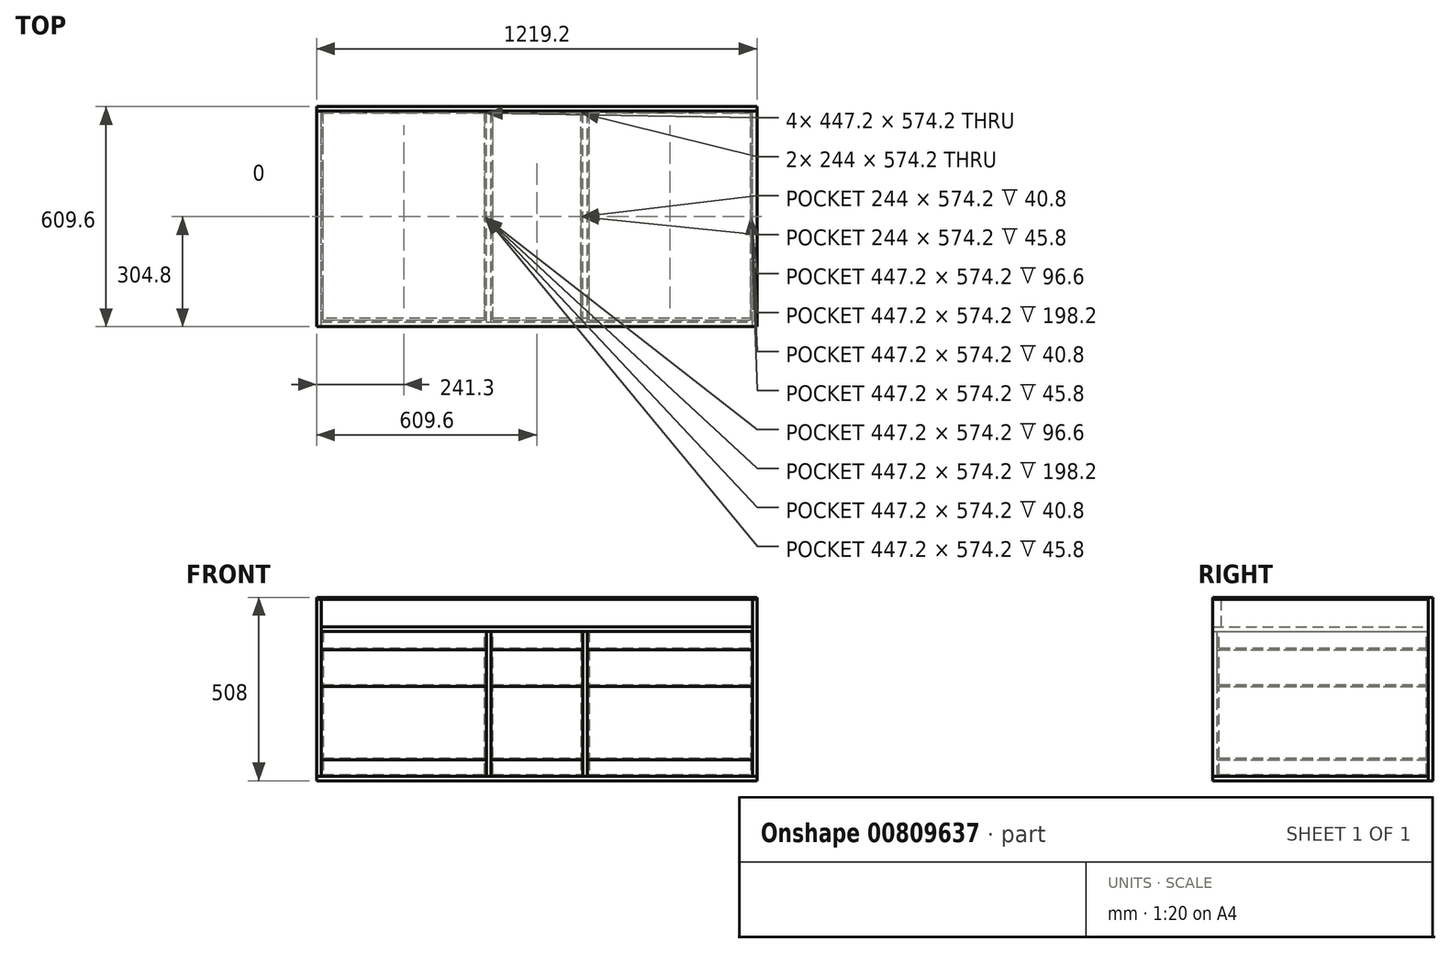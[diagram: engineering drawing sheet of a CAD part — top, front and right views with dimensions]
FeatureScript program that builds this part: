
annotation { "Feature Type Name" : "Feature", "Feature Type Description" : "" }
export const myFeature = defineFeature(function(context is Context, id is Id, definition is map)
    precondition{}
    {
        {
            assignVariable(context, id + "F0", {"name" : "thinwood", "anyValue" : 5 * mm});
        }
        {
            assignVariable(context, id + "F1", {"name" : "thickwood", "anyValue" : 12.7 * mm});
        }
        {
            assignVariable(context, id + "F2", {"name" : "cartlength", "anyValue" : 1219.2 * mm});
        }
        {
            assignVariable(context, id + "F3", {"name" : "cartwidth", "anyValue" : 609.6 * mm});
        }
        {
            assignVariable(context, id + "F4", {"name" : "drawerdepth", "anyValue" : getVariable(context, 'cartwidth') - 2 * getVariable(context, 'thickwood')});
        }
        {
            var Q0;
            Q0=qCreatedBy(makeId("Front.planeOp"),FACE);
            var sketch = newSketch(context, id + "F5", { "sketchPlane" : qUnion([Q0])});
            skLineSegment(sketch, "E0.bottom", {"start": v(609.6, 254) * mm, "end": v(-609.6, 254) * mm});
            skLineSegment(sketch, "E0.top", {"start": v(609.6, -254) * mm, "end": v(-609.6, -254) * mm});
            skLineSegment(sketch, "E0.left", {"start": v(609.6, 254) * mm, "end": v(609.6, -254) * mm});
            skLineSegment(sketch, "E0.right", {"start": v(-609.6, 254) * mm, "end": v(-609.6, -254) * mm});
            skPoint(sketch, "E0.middle", {"position": v(0, 0) * mm});
            skLineSegment(sketch, "E1", {"start": v(-139.7, -254) * mm, "end": v(-139.7, 254) * mm});
            skLineSegment(sketch, "E2", {"start": v(-127, -254) * mm, "end": v(-127, 254) * mm});
            skLineSegment(sketch, "E3.bottom", {"start": v(-596.9, 249) * mm, "end": v(596.9, 249) * mm});
            skLineSegment(sketch, "E3.left", {"start": v(-596.9, 249) * mm, "end": v(-596.9, -241.3) * mm});
            skLineSegment(sketch, "E3.right", {"start": v(596.9, 249) * mm, "end": v(596.9, -241.3) * mm});
            skLineSegment(sketch, "E4", {"start": v(-609.6, 160.1) * mm, "end": v(609.6, 160.1) * mm});
            skLineSegment(sketch, "E5", {"start": v(-609.6, 109.3) * mm, "end": v(609.6, 109.3) * mm});
            skLineSegment(sketch, "E6", {"start": v(-609.6, 7.7) * mm, "end": v(609.6, 7.7) * mm});
            skLineSegment(sketch, "E7", {"start": v(-609.6, -195.5) * mm, "end": v(596.9, -195.5) * mm});
            skLineSegment(sketch, "E8", {"start": v(-596.9, 212.06) * mm, "end": v(-133.35, 212.06) * mm, "construction": true});
            skLineSegment(sketch, "E9", {"start": v(-133.35, 212.06) * mm, "end": v(133.35, 212.06) * mm, "construction": true});
            skLineSegment(sketch, "E10", {"start": v(133.35, 212.06) * mm, "end": v(596.9, 212.06) * mm, "construction": true});
            skLineSegment(sketch, "E11", {"start": v(-596.9, -241.3) * mm, "end": v(596.9, -241.3) * mm});
            skLineSegment(sketch, "E12", {"start": v(-596.9, 249) * mm, "end": v(-609.6, 249) * mm});
            skLineSegment(sketch, "E13", {"start": v(596.9, 249) * mm, "end": v(609.6, 249) * mm});
            skLineSegment(sketch, "E14", {"start": v(596.9, -241.3) * mm, "end": v(609.6, -241.3) * mm});
            skLineSegment(sketch, "E15", {"start": v(-596.9, -241.3) * mm, "end": v(-609.6, -241.3) * mm});
            skLineSegment(sketch, "E16", {"start": v(-133.35, 202.82) * mm, "end": v(-139.7, 202.82) * mm, "construction": true});
            skLineSegment(sketch, "E17", {"start": v(-133.35, 202.82) * mm, "end": v(-127, 202.82) * mm, "construction": true});
            skLineSegment(sketch, "E18", {"start": v(127, 254) * mm, "end": v(127, -254) * mm});
            skLineSegment(sketch, "E19", {"start": v(139.7, 254) * mm, "end": v(139.7, -254) * mm});
            skLineSegment(sketch, "E20", {"start": v(133.35, 195.05) * mm, "end": v(127, 195.05) * mm, "construction": true});
            skLineSegment(sketch, "E21", {"start": v(133.35, 195.05) * mm, "end": v(139.7, 195.05) * mm, "construction": true});
            skLineSegment(sketch, "E22", {"start": v(-609.6, 172.8) * mm, "end": v(609.6, 172.8) * mm});
            skSolve(sketch);
        }
        {
            var Q0;
            {var subQ0=sQuery(id+"F5.wireOp",EDGE,"E12");Q0=makeQuery(id+"F5.imprint","IMPRINT",FACE,{"disambiguationData":[TD([[makeQuery(id+"F5.imprint","IMPRINT",EDGE,{"derivedFrom":subQ0}),-1.0]])]});}
            var Q1;
            {var subQ0=sQuery(id+"F5.wireOp",EDGE,"E1");var subQ1=sQuery(id+"F5.wireOp",EDGE,"E0.bottom");var subQ2=makeQuery(id+"F5.imprint","INTERSECT",VERTEX,{"derivedFrom":[subQ1,subQ0]});Q1=makeQuery(id+"F5.imprint","IMPRINT",FACE,{"disambiguationData":[TD([[makeQuery(id+"F5.imprint","IMPRINT",EDGE,{"disambiguationData":[TD([[subQ2,1.0]])],"derivedFrom":subQ1}),1.0]])]});}
            var Q2;
            {var subQ0=sQuery(id+"F5.wireOp",EDGE,"E2");var subQ1=sQuery(id+"F5.wireOp",EDGE,"E0.bottom");var subQ2=makeQuery(id+"F5.imprint","INTERSECT",VERTEX,{"derivedFrom":[subQ1,subQ0]});Q2=makeQuery(id+"F5.imprint","IMPRINT",FACE,{"disambiguationData":[TD([[makeQuery(id+"F5.imprint","IMPRINT",EDGE,{"disambiguationData":[TD([[subQ2,1.0]])],"derivedFrom":subQ1}),1.0]])]});}
            var Q3;
            {var subQ0=sQuery(id+"F5.wireOp",EDGE,"E18");var subQ1=sQuery(id+"F5.wireOp",EDGE,"E0.bottom");var subQ2=makeQuery(id+"F5.imprint","INTERSECT",VERTEX,{"derivedFrom":[subQ1,subQ0]});Q3=makeQuery(id+"F5.imprint","IMPRINT",FACE,{"disambiguationData":[TD([[makeQuery(id+"F5.imprint","IMPRINT",EDGE,{"disambiguationData":[TD([[subQ2,1.0]])],"derivedFrom":subQ1}),1.0]])]});}
            var Q4;
            {var subQ0=sQuery(id+"F5.wireOp",EDGE,"E13");Q4=makeQuery(id+"F5.imprint","IMPRINT",FACE,{"disambiguationData":[TD([[makeQuery(id+"F5.imprint","IMPRINT",EDGE,{"derivedFrom":subQ0}),1.0]])]});}
            extrude(context, id + "F6", {"entities" : qUnion([Q0, Q1, Q2, Q3, Q4]), "depth" : getVariable(context, 'cartwidth') - getVariable(context, 'thickwood'), "offsetDistance" : 25.4 * mm});
        }
        {
            var Q0;
            {var subQ3=sQuery(id+"F5.wireOp",EDGE,"E15");Q0=makeQuery(id+"F5.imprint","IMPRINT",FACE,{"disambiguationData":[TD([[makeQuery(id+"F5.imprint","IMPRINT",EDGE,{"derivedFrom":subQ3}),-1.0]])]});}
            var Q1;
            {var subQ0=sQuery(id+"F5.wireOp",EDGE,"E5");var subQ1=sQuery(id+"F5.wireOp",EDGE,"E0.right");var subQ2=makeQuery(id+"F5.imprint","INTERSECT",VERTEX,{"derivedFrom":[subQ1,subQ0]});Q1=makeQuery(id+"F5.imprint","IMPRINT",FACE,{"disambiguationData":[TD([[makeQuery(id+"F5.imprint","IMPRINT",EDGE,{"disambiguationData":[TD([[subQ2,-1.0]])],"derivedFrom":subQ1}),1.0]])]});}
            var Q2;
            {var subQ0=sQuery(id+"F5.wireOp",EDGE,"E4");var subQ1=sQuery(id+"F5.wireOp",EDGE,"E0.right");var subQ2=makeQuery(id+"F5.imprint","INTERSECT",VERTEX,{"derivedFrom":[subQ1,subQ0]});Q2=makeQuery(id+"F5.imprint","IMPRINT",FACE,{"disambiguationData":[TD([[makeQuery(id+"F5.imprint","IMPRINT",EDGE,{"disambiguationData":[TD([[subQ2,-1.0]])],"derivedFrom":subQ1}),1.0]])]});}
            var Q3;
            {var subQ3=sQuery(id+"F5.wireOp",EDGE,"E12");Q3=makeQuery(id+"F5.imprint","IMPRINT",FACE,{"disambiguationData":[TD([[makeQuery(id+"F5.imprint","IMPRINT",EDGE,{"derivedFrom":subQ3}),1.0]])]});}
            var Q4;
            {var subQ0=sQuery(id+"F5.wireOp",EDGE,"E6");var subQ1=sQuery(id+"F5.wireOp",EDGE,"E0.right");var subQ2=makeQuery(id+"F5.imprint","INTERSECT",VERTEX,{"derivedFrom":[subQ1,subQ0]});Q4=makeQuery(id+"F5.imprint","IMPRINT",FACE,{"disambiguationData":[TD([[makeQuery(id+"F5.imprint","IMPRINT",EDGE,{"disambiguationData":[TD([[subQ2,-1.0]])],"derivedFrom":subQ1}),1.0]])]});}
            var Q5;
            {var subQ0=sQuery(id+"F5.wireOp",EDGE,"E4");var subQ1=sQuery(id+"F5.wireOp",EDGE,"E0.right");var subQ2=makeQuery(id+"F5.imprint","INTERSECT",VERTEX,{"derivedFrom":[subQ1,subQ0]});Q5=makeQuery(id+"F5.imprint","IMPRINT",FACE,{"disambiguationData":[TD([[makeQuery(id+"F5.imprint","IMPRINT",EDGE,{"disambiguationData":[TD([[subQ2,1.0]])],"derivedFrom":subQ1}),1.0]])]});}
            extrude(context, id + "F7", {"entities" : qUnion([Q0, Q1, Q2, Q3, Q4, Q5]), "depth" : getVariable(context, 'cartwidth') - getVariable(context, 'thickwood'), "offsetDistance" : 25.4 * mm});
        }
        {
            var Q0;
            {var subQ0=sQuery(id+"F5.wireOp",EDGE,"E4");var subQ1=sQuery(id+"F5.wireOp",EDGE,"E0.left");var subQ2=makeQuery(id+"F5.imprint","INTERSECT",VERTEX,{"derivedFrom":[subQ1,subQ0]});Q0=makeQuery(id+"F5.imprint","IMPRINT",FACE,{"disambiguationData":[TD([[makeQuery(id+"F5.imprint","IMPRINT",EDGE,{"disambiguationData":[TD([[subQ2,-1.0]])],"derivedFrom":subQ1}),-1.0]])]});}
            var Q1;
            {var subQ0=sQuery(id+"F5.wireOp",EDGE,"E5");var subQ1=sQuery(id+"F5.wireOp",EDGE,"E0.left");var subQ2=makeQuery(id+"F5.imprint","INTERSECT",VERTEX,{"derivedFrom":[subQ1,subQ0]});Q1=makeQuery(id+"F5.imprint","IMPRINT",FACE,{"disambiguationData":[TD([[makeQuery(id+"F5.imprint","IMPRINT",EDGE,{"disambiguationData":[TD([[subQ2,-1.0]])],"derivedFrom":subQ1}),-1.0]])]});}
            var Q2;
            {var subQ3=sQuery(id+"F5.wireOp",EDGE,"E13");Q2=makeQuery(id+"F5.imprint","IMPRINT",FACE,{"disambiguationData":[TD([[makeQuery(id+"F5.imprint","IMPRINT",EDGE,{"derivedFrom":subQ3}),-1.0]])]});}
            var Q3;
            {var subQ6=sQuery(id+"F5.wireOp",EDGE,"E14");Q3=makeQuery(id+"F5.imprint","IMPRINT",FACE,{"disambiguationData":[TD([[makeQuery(id+"F5.imprint","IMPRINT",EDGE,{"derivedFrom":subQ6}),1.0]])]});}
            var Q4;
            {var subQ0=sQuery(id+"F5.wireOp",EDGE,"E4");var subQ1=sQuery(id+"F5.wireOp",EDGE,"E0.left");var subQ2=makeQuery(id+"F5.imprint","INTERSECT",VERTEX,{"derivedFrom":[subQ1,subQ0]});Q4=makeQuery(id+"F5.imprint","IMPRINT",FACE,{"disambiguationData":[TD([[makeQuery(id+"F5.imprint","IMPRINT",EDGE,{"disambiguationData":[TD([[subQ2,1.0]])],"derivedFrom":subQ1}),-1.0]])]});}
            extrude(context, id + "F8", {"entities" : qUnion([Q0, Q1, Q2, Q3, Q4]), "depth" : getVariable(context, 'cartwidth') - getVariable(context, 'thickwood'), "offsetDistance" : 25.4 * mm});
        }
        {
            var Q0;
            {var subQ0=sQuery(id+"F5.wireOp",EDGE,"E5");var subQ1=sQuery(id+"F5.wireOp",EDGE,"E1");var subQ2=makeQuery(id+"F5.imprint","INTERSECT",VERTEX,{"derivedFrom":[subQ1,subQ0]});Q0=makeQuery(id+"F5.imprint","IMPRINT",FACE,{"disambiguationData":[TD([[makeQuery(id+"F5.imprint","IMPRINT",EDGE,{"disambiguationData":[TD([[subQ2,-1.0]])],"derivedFrom":subQ1}),-1.0]])]});}
            var Q1;
            {var subQ0=sQuery(id+"F5.wireOp",EDGE,"E6");var subQ1=sQuery(id+"F5.wireOp",EDGE,"E1");var subQ2=makeQuery(id+"F5.imprint","INTERSECT",VERTEX,{"derivedFrom":[subQ1,subQ0]});Q1=makeQuery(id+"F5.imprint","IMPRINT",FACE,{"disambiguationData":[TD([[makeQuery(id+"F5.imprint","IMPRINT",EDGE,{"disambiguationData":[TD([[subQ2,-1.0]])],"derivedFrom":subQ1}),-1.0]])]});}
            var Q2;
            {var subQ0=sQuery(id+"F5.wireOp",EDGE,"E7");var subQ1=sQuery(id+"F5.wireOp",EDGE,"E1");var subQ2=makeQuery(id+"F5.imprint","INTERSECT",VERTEX,{"derivedFrom":[subQ1,subQ0]});Q2=makeQuery(id+"F5.imprint","IMPRINT",FACE,{"disambiguationData":[TD([[makeQuery(id+"F5.imprint","IMPRINT",EDGE,{"disambiguationData":[TD([[subQ2,-1.0]])],"derivedFrom":subQ1}),-1.0]])]});}
            var Q3;
            {var subQ0=sQuery(id+"F5.wireOp",EDGE,"E11");var subQ1=sQuery(id+"F5.wireOp",EDGE,"E1");var subQ2=makeQuery(id+"F5.imprint","INTERSECT",VERTEX,{"derivedFrom":[subQ1,subQ0]});Q3=makeQuery(id+"F5.imprint","IMPRINT",FACE,{"disambiguationData":[TD([[makeQuery(id+"F5.imprint","IMPRINT",EDGE,{"disambiguationData":[TD([[subQ2,-1.0]])],"derivedFrom":subQ1}),-1.0]])]});}
            extrude(context, id + "F9", {"entities" : qUnion([Q0, Q1, Q2, Q3]), "depth" : getVariable(context, 'cartwidth') - 2 * getVariable(context, 'thickwood'), "offsetDistance" : 25.4 * mm});
        }
        {
            var Q0;
            {var subQ0=sQuery(id+"F5.wireOp",EDGE,"E18");var subQ1=sQuery(id+"F5.wireOp",EDGE,"E7");var subQ2=makeQuery(id+"F5.imprint","INTERSECT",VERTEX,{"derivedFrom":[subQ1,subQ0]});Q0=makeQuery(id+"F5.imprint","IMPRINT",FACE,{"disambiguationData":[TD([[makeQuery(id+"F5.imprint","IMPRINT",EDGE,{"disambiguationData":[TD([[subQ2,-1.0]])],"derivedFrom":subQ1}),-1.0]])]});}
            var Q1;
            {var subQ0=sQuery(id+"F5.wireOp",EDGE,"E18");var subQ1=sQuery(id+"F5.wireOp",EDGE,"E6");var subQ2=makeQuery(id+"F5.imprint","INTERSECT",VERTEX,{"derivedFrom":[subQ1,subQ0]});Q1=makeQuery(id+"F5.imprint","IMPRINT",FACE,{"disambiguationData":[TD([[makeQuery(id+"F5.imprint","IMPRINT",EDGE,{"disambiguationData":[TD([[subQ2,-1.0]])],"derivedFrom":subQ1}),-1.0]])]});}
            var Q2;
            {var subQ0=sQuery(id+"F5.wireOp",EDGE,"E18");var subQ1=sQuery(id+"F5.wireOp",EDGE,"E5");var subQ2=makeQuery(id+"F5.imprint","INTERSECT",VERTEX,{"derivedFrom":[subQ1,subQ0]});Q2=makeQuery(id+"F5.imprint","IMPRINT",FACE,{"disambiguationData":[TD([[makeQuery(id+"F5.imprint","IMPRINT",EDGE,{"disambiguationData":[TD([[subQ2,-1.0]])],"derivedFrom":subQ1}),-1.0]])]});}
            var Q3;
            {var subQ0=sQuery(id+"F5.wireOp",EDGE,"E18");var subQ1=sQuery(id+"F5.wireOp",EDGE,"E4");var subQ2=makeQuery(id+"F5.imprint","INTERSECT",VERTEX,{"derivedFrom":[subQ1,subQ0]});Q3=makeQuery(id+"F5.imprint","IMPRINT",FACE,{"disambiguationData":[TD([[makeQuery(id+"F5.imprint","IMPRINT",EDGE,{"disambiguationData":[TD([[subQ2,-1.0]])],"derivedFrom":subQ1}),-1.0]])]});}
            extrude(context, id + "F10", {"entities" : qUnion([Q0, Q1, Q2, Q3]), "depth" : getVariable(context, 'cartwidth') - 2 * getVariable(context, 'thickwood'), "offsetDistance" : 25.4 * mm});
        }
        {
            var Q0;
            {var subQ7=sQuery(id+"F5.wireOp",EDGE,"E15");Q0=makeQuery(id+"F5.imprint","IMPRINT",FACE,{"disambiguationData":[TD([[makeQuery(id+"F5.imprint","IMPRINT",EDGE,{"derivedFrom":subQ7}),1.0]])]});}
            var Q1;
            {var subQ0=sQuery(id+"F5.wireOp",EDGE,"E1");var subQ1=sQuery(id+"F5.wireOp",EDGE,"E0.top");var subQ2=makeQuery(id+"F5.imprint","INTERSECT",VERTEX,{"derivedFrom":[subQ1,subQ0]});Q1=makeQuery(id+"F5.imprint","IMPRINT",FACE,{"disambiguationData":[TD([[makeQuery(id+"F5.imprint","IMPRINT",EDGE,{"disambiguationData":[TD([[subQ2,1.0]])],"derivedFrom":subQ1}),-1.0]])]});}
            var Q2;
            {var subQ0=sQuery(id+"F5.wireOp",EDGE,"E2");var subQ1=sQuery(id+"F5.wireOp",EDGE,"E0.top");var subQ2=makeQuery(id+"F5.imprint","INTERSECT",VERTEX,{"derivedFrom":[subQ1,subQ0]});Q2=makeQuery(id+"F5.imprint","IMPRINT",FACE,{"disambiguationData":[TD([[makeQuery(id+"F5.imprint","IMPRINT",EDGE,{"disambiguationData":[TD([[subQ2,1.0]])],"derivedFrom":subQ1}),-1.0]])]});}
            var Q3;
            {var subQ0=sQuery(id+"F5.wireOp",EDGE,"E18");var subQ1=sQuery(id+"F5.wireOp",EDGE,"E0.top");var subQ2=makeQuery(id+"F5.imprint","INTERSECT",VERTEX,{"derivedFrom":[subQ1,subQ0]});Q3=makeQuery(id+"F5.imprint","IMPRINT",FACE,{"disambiguationData":[TD([[makeQuery(id+"F5.imprint","IMPRINT",EDGE,{"disambiguationData":[TD([[subQ2,1.0]])],"derivedFrom":subQ1}),-1.0]])]});}
            var Q4;
            {var subQ0=sQuery(id+"F5.wireOp",EDGE,"E14");Q4=makeQuery(id+"F5.imprint","IMPRINT",FACE,{"disambiguationData":[TD([[makeQuery(id+"F5.imprint","IMPRINT",EDGE,{"derivedFrom":subQ0}),-1.0]])]});}
            var Q5;
            Q5=makeQuery(id+"F9.opExtrude","CAP_FACE",FACE,{"disambiguationData":[OSD([sQuery(id+"F5.wireOp",EDGE,"E1"),sQuery(id+"F5.wireOp",EDGE,"E2"),sQuery(id+"F5.wireOp",EDGE,"E3.bottom"),sQuery(id+"F5.wireOp",EDGE,"E11")])],"isStart":false});
            extrude(context, id + "F11", {"entities" : qUnion([Q0, Q1, Q2, Q3, Q4]), "depth" : getVariable(context, 'cartwidth') - getVariable(context, 'thickwood'), "endBoundEntityFace" : qUnion([Q5]), "offsetDistance" : 25.4 * mm});
        }
        {
            var Q0;
            {var subQ0=sQuery(id+"F5.wireOp",EDGE,"E4");var subQ1=sQuery(id+"F5.wireOp",EDGE,"E2");var subQ2=makeQuery(id+"F5.imprint","INTERSECT",VERTEX,{"derivedFrom":[subQ1,subQ0]});Q0=makeQuery(id+"F5.imprint","IMPRINT",FACE,{"disambiguationData":[TD([[makeQuery(id+"F5.imprint","IMPRINT",EDGE,{"disambiguationData":[TD([[subQ2,-1.0]])],"derivedFrom":subQ1}),-1.0]])]});}
            var Q1;
            {var subQ0=sQuery(id+"F5.wireOp",EDGE,"E11");var subQ1=sQuery(id+"F5.wireOp",EDGE,"E2");var subQ2=makeQuery(id+"F5.imprint","INTERSECT",VERTEX,{"derivedFrom":[subQ1,subQ0]});Q1=makeQuery(id+"F5.imprint","IMPRINT",FACE,{"disambiguationData":[TD([[makeQuery(id+"F5.imprint","IMPRINT",EDGE,{"disambiguationData":[TD([[subQ2,-1.0]])],"derivedFrom":subQ1}),-1.0]])]});}
            var Q2;
            {var subQ0=sQuery(id+"F5.wireOp",EDGE,"E4");var subQ1=sQuery(id+"F5.wireOp",EDGE,"E3.right");var subQ2=makeQuery(id+"F5.imprint","INTERSECT",VERTEX,{"derivedFrom":[subQ1,subQ0]});Q2=makeQuery(id+"F5.imprint","IMPRINT",FACE,{"disambiguationData":[TD([[makeQuery(id+"F5.imprint","IMPRINT",EDGE,{"disambiguationData":[TD([[subQ2,-1.0]])],"derivedFrom":subQ1}),-1.0]])]});}
            var Q3;
            {var subQ0=sQuery(id+"F5.wireOp",EDGE,"E6");var subQ1=sQuery(id+"F5.wireOp",EDGE,"E1");var subQ2=makeQuery(id+"F5.imprint","INTERSECT",VERTEX,{"derivedFrom":[subQ1,subQ0]});Q3=makeQuery(id+"F5.imprint","IMPRINT",FACE,{"disambiguationData":[TD([[makeQuery(id+"F5.imprint","IMPRINT",EDGE,{"disambiguationData":[TD([[subQ2,-1.0]])],"derivedFrom":subQ1}),1.0]])]});}
            var Q4;
            {var subQ1=sQuery(id+"F5.wireOp",EDGE,"E3.right");var subQ3=sQuery(id+"F5.wireOp",EDGE,"E7");var subQ4=makeQuery(id+"F5.imprint","INTERSECT",VERTEX,{"derivedFrom":[subQ1,subQ3]});Q4=makeQuery(id+"F5.imprint","IMPRINT",FACE,{"disambiguationData":[TD([[makeQuery(id+"F5.imprint","IMPRINT",EDGE,{"disambiguationData":[TD([[subQ4,1.0]])],"derivedFrom":subQ3}),-1.0]])]});}
            var Q5;
            {var subQ0=sQuery(id+"F5.wireOp",EDGE,"E5");var subQ1=sQuery(id+"F5.wireOp",EDGE,"E3.right");var subQ2=makeQuery(id+"F5.imprint","INTERSECT",VERTEX,{"derivedFrom":[subQ1,subQ0]});Q5=makeQuery(id+"F5.imprint","IMPRINT",FACE,{"disambiguationData":[TD([[makeQuery(id+"F5.imprint","IMPRINT",EDGE,{"disambiguationData":[TD([[subQ2,-1.0]])],"derivedFrom":subQ1}),-1.0]])]});}
            var Q6;
            {var subQ0=sQuery(id+"F5.wireOp",EDGE,"E18");var subQ1=sQuery(id+"F5.wireOp",EDGE,"E4");var subQ2=makeQuery(id+"F5.imprint","INTERSECT",VERTEX,{"derivedFrom":[subQ1,subQ0]});Q6=makeQuery(id+"F5.imprint","IMPRINT",FACE,{"disambiguationData":[TD([[makeQuery(id+"F5.imprint","IMPRINT",EDGE,{"disambiguationData":[TD([[subQ2,-1.0]])],"derivedFrom":subQ1}),-1.0]])]});}
            var Q7;
            {var subQ0=sQuery(id+"F5.wireOp",EDGE,"E11");var subQ1=sQuery(id+"F5.wireOp",EDGE,"E1");var subQ2=makeQuery(id+"F5.imprint","INTERSECT",VERTEX,{"derivedFrom":[subQ1,subQ0]});Q7=makeQuery(id+"F5.imprint","IMPRINT",FACE,{"disambiguationData":[TD([[makeQuery(id+"F5.imprint","IMPRINT",EDGE,{"disambiguationData":[TD([[subQ2,-1.0]])],"derivedFrom":subQ1}),1.0]])]});}
            var Q8;
            {var subQ0=sQuery(id+"F5.wireOp",EDGE,"E7");var subQ1=sQuery(id+"F5.wireOp",EDGE,"E2");var subQ2=makeQuery(id+"F5.imprint","INTERSECT",VERTEX,{"derivedFrom":[subQ1,subQ0]});Q8=makeQuery(id+"F5.imprint","IMPRINT",FACE,{"disambiguationData":[TD([[makeQuery(id+"F5.imprint","IMPRINT",EDGE,{"disambiguationData":[TD([[subQ2,-1.0]])],"derivedFrom":subQ1}),-1.0]])]});}
            var Q9;
            {var subQ0=sQuery(id+"F5.wireOp",EDGE,"E4");var subQ1=sQuery(id+"F5.wireOp",EDGE,"E1");var subQ2=makeQuery(id+"F5.imprint","INTERSECT",VERTEX,{"derivedFrom":[subQ1,subQ0]});Q9=makeQuery(id+"F5.imprint","IMPRINT",FACE,{"disambiguationData":[TD([[makeQuery(id+"F5.imprint","IMPRINT",EDGE,{"disambiguationData":[TD([[subQ2,-1.0]])],"derivedFrom":subQ1}),1.0]])]});}
            var Q10;
            {var subQ0=sQuery(id+"F5.wireOp",EDGE,"E7");var subQ1=sQuery(id+"F5.wireOp",EDGE,"E1");var subQ2=makeQuery(id+"F5.imprint","INTERSECT",VERTEX,{"derivedFrom":[subQ1,subQ0]});Q10=makeQuery(id+"F5.imprint","IMPRINT",FACE,{"disambiguationData":[TD([[makeQuery(id+"F5.imprint","IMPRINT",EDGE,{"disambiguationData":[TD([[subQ2,-1.0]])],"derivedFrom":subQ1}),-1.0]])]});}
            var Q11;
            {var subQ0=sQuery(id+"F5.wireOp",EDGE,"E6");var subQ1=sQuery(id+"F5.wireOp",EDGE,"E1");var subQ2=makeQuery(id+"F5.imprint","INTERSECT",VERTEX,{"derivedFrom":[subQ1,subQ0]});Q11=makeQuery(id+"F5.imprint","IMPRINT",FACE,{"disambiguationData":[TD([[makeQuery(id+"F5.imprint","IMPRINT",EDGE,{"disambiguationData":[TD([[subQ2,-1.0]])],"derivedFrom":subQ1}),-1.0]])]});}
            var Q12;
            {var subQ0=sQuery(id+"F5.wireOp",EDGE,"E18");var subQ1=sQuery(id+"F5.wireOp",EDGE,"E7");var subQ2=makeQuery(id+"F5.imprint","INTERSECT",VERTEX,{"derivedFrom":[subQ1,subQ0]});Q12=makeQuery(id+"F5.imprint","IMPRINT",FACE,{"disambiguationData":[TD([[makeQuery(id+"F5.imprint","IMPRINT",EDGE,{"disambiguationData":[TD([[subQ2,-1.0]])],"derivedFrom":subQ1}),-1.0]])]});}
            var Q13;
            {var subQ0=sQuery(id+"F5.wireOp",EDGE,"E5");var subQ1=sQuery(id+"F5.wireOp",EDGE,"E2");var subQ2=makeQuery(id+"F5.imprint","INTERSECT",VERTEX,{"derivedFrom":[subQ1,subQ0]});Q13=makeQuery(id+"F5.imprint","IMPRINT",FACE,{"disambiguationData":[TD([[makeQuery(id+"F5.imprint","IMPRINT",EDGE,{"disambiguationData":[TD([[subQ2,-1.0]])],"derivedFrom":subQ1}),-1.0]])]});}
            var Q14;
            {var subQ0=sQuery(id+"F5.wireOp",EDGE,"E7");var subQ1=sQuery(id+"F5.wireOp",EDGE,"E1");var subQ2=makeQuery(id+"F5.imprint","INTERSECT",VERTEX,{"derivedFrom":[subQ1,subQ0]});Q14=makeQuery(id+"F5.imprint","IMPRINT",FACE,{"disambiguationData":[TD([[makeQuery(id+"F5.imprint","IMPRINT",EDGE,{"disambiguationData":[TD([[subQ2,-1.0]])],"derivedFrom":subQ1}),1.0]])]});}
            var Q15;
            {var subQ0=sQuery(id+"F5.wireOp",EDGE,"E7");var subQ1=sQuery(id+"F5.wireOp",EDGE,"E3.right");var subQ2=makeQuery(id+"F5.imprint","INTERSECT",VERTEX,{"derivedFrom":[subQ1,subQ0]});Q15=makeQuery(id+"F5.imprint","IMPRINT",FACE,{"disambiguationData":[TD([[makeQuery(id+"F5.imprint","IMPRINT",EDGE,{"disambiguationData":[TD([[subQ2,1.0]])],"derivedFrom":subQ1}),-1.0]])]});}
            var Q16;
            {var subQ0=sQuery(id+"F5.wireOp",EDGE,"E6");var subQ1=sQuery(id+"F5.wireOp",EDGE,"E2");var subQ2=makeQuery(id+"F5.imprint","INTERSECT",VERTEX,{"derivedFrom":[subQ1,subQ0]});Q16=makeQuery(id+"F5.imprint","IMPRINT",FACE,{"disambiguationData":[TD([[makeQuery(id+"F5.imprint","IMPRINT",EDGE,{"disambiguationData":[TD([[subQ2,-1.0]])],"derivedFrom":subQ1}),-1.0]])]});}
            var Q17;
            {var subQ0=sQuery(id+"F5.wireOp",EDGE,"E5");var subQ1=sQuery(id+"F5.wireOp",EDGE,"E1");var subQ2=makeQuery(id+"F5.imprint","INTERSECT",VERTEX,{"derivedFrom":[subQ1,subQ0]});Q17=makeQuery(id+"F5.imprint","IMPRINT",FACE,{"disambiguationData":[TD([[makeQuery(id+"F5.imprint","IMPRINT",EDGE,{"disambiguationData":[TD([[subQ2,-1.0]])],"derivedFrom":subQ1}),1.0]])]});}
            var Q18;
            {var subQ0=sQuery(id+"F5.wireOp",EDGE,"E18");var subQ1=sQuery(id+"F5.wireOp",EDGE,"E6");var subQ2=makeQuery(id+"F5.imprint","INTERSECT",VERTEX,{"derivedFrom":[subQ1,subQ0]});Q18=makeQuery(id+"F5.imprint","IMPRINT",FACE,{"disambiguationData":[TD([[makeQuery(id+"F5.imprint","IMPRINT",EDGE,{"disambiguationData":[TD([[subQ2,-1.0]])],"derivedFrom":subQ1}),-1.0]])]});}
            var Q19;
            {var subQ0=sQuery(id+"F5.wireOp",EDGE,"E3.right");var subQ5=sQuery(id+"F5.wireOp",EDGE,"E4");var subQ7=makeQuery(id+"F5.imprint","INTERSECT",VERTEX,{"derivedFrom":[subQ0,subQ5]});Q19=makeQuery(id+"F5.imprint","IMPRINT",FACE,{"disambiguationData":[TD([[makeQuery(id+"F5.imprint","IMPRINT",EDGE,{"disambiguationData":[TD([[subQ7,1.0]])],"derivedFrom":subQ5}),1.0]])]});}
            var Q20;
            {var subQ0=sQuery(id+"F5.wireOp",EDGE,"E18");var subQ1=sQuery(id+"F5.wireOp",EDGE,"E5");var subQ2=makeQuery(id+"F5.imprint","INTERSECT",VERTEX,{"derivedFrom":[subQ1,subQ0]});Q20=makeQuery(id+"F5.imprint","IMPRINT",FACE,{"disambiguationData":[TD([[makeQuery(id+"F5.imprint","IMPRINT",EDGE,{"disambiguationData":[TD([[subQ2,-1.0]])],"derivedFrom":subQ1}),-1.0]])]});}
            var Q21;
            {var subQ0=sQuery(id+"F5.wireOp",EDGE,"E5");var subQ1=sQuery(id+"F5.wireOp",EDGE,"E1");var subQ2=makeQuery(id+"F5.imprint","INTERSECT",VERTEX,{"derivedFrom":[subQ1,subQ0]});Q21=makeQuery(id+"F5.imprint","IMPRINT",FACE,{"disambiguationData":[TD([[makeQuery(id+"F5.imprint","IMPRINT",EDGE,{"disambiguationData":[TD([[subQ2,-1.0]])],"derivedFrom":subQ1}),-1.0]])]});}
            var Q22;
            {var subQ0=sQuery(id+"F5.wireOp",EDGE,"E11");var subQ1=sQuery(id+"F5.wireOp",EDGE,"E1");var subQ2=makeQuery(id+"F5.imprint","INTERSECT",VERTEX,{"derivedFrom":[subQ1,subQ0]});Q22=makeQuery(id+"F5.imprint","IMPRINT",FACE,{"disambiguationData":[TD([[makeQuery(id+"F5.imprint","IMPRINT",EDGE,{"disambiguationData":[TD([[subQ2,-1.0]])],"derivedFrom":subQ1}),-1.0]])]});}
            var Q23;
            {var subQ0=sQuery(id+"F5.wireOp",EDGE,"E5");var subQ1=sQuery(id+"F5.wireOp",EDGE,"E0.right");var subQ2=makeQuery(id+"F5.imprint","INTERSECT",VERTEX,{"derivedFrom":[subQ1,subQ0]});Q23=makeQuery(id+"F5.imprint","IMPRINT",FACE,{"disambiguationData":[TD([[makeQuery(id+"F5.imprint","IMPRINT",EDGE,{"disambiguationData":[TD([[subQ2,-1.0]])],"derivedFrom":subQ1}),1.0]])]});}
            var Q24;
            {var subQ0=sQuery(id+"F5.wireOp",EDGE,"E14");Q24=makeQuery(id+"F5.imprint","IMPRINT",FACE,{"disambiguationData":[TD([[makeQuery(id+"F5.imprint","IMPRINT",EDGE,{"derivedFrom":subQ0}),-1.0]])]});}
            var Q25;
            {var subQ0=sQuery(id+"F5.wireOp",EDGE,"E4");var subQ1=sQuery(id+"F5.wireOp",EDGE,"E0.right");var subQ2=makeQuery(id+"F5.imprint","INTERSECT",VERTEX,{"derivedFrom":[subQ1,subQ0]});Q25=makeQuery(id+"F5.imprint","IMPRINT",FACE,{"disambiguationData":[TD([[makeQuery(id+"F5.imprint","IMPRINT",EDGE,{"disambiguationData":[TD([[subQ2,-1.0]])],"derivedFrom":subQ1}),1.0]])]});}
            var Q26;
            {var subQ0=sQuery(id+"F5.wireOp",EDGE,"E1");var subQ1=sQuery(id+"F5.wireOp",EDGE,"E0.top");var subQ2=makeQuery(id+"F5.imprint","INTERSECT",VERTEX,{"derivedFrom":[subQ1,subQ0]});Q26=makeQuery(id+"F5.imprint","IMPRINT",FACE,{"disambiguationData":[TD([[makeQuery(id+"F5.imprint","IMPRINT",EDGE,{"disambiguationData":[TD([[subQ2,1.0]])],"derivedFrom":subQ1}),-1.0]])]});}
            var Q27;
            {var subQ0=sQuery(id+"F5.wireOp",EDGE,"E5");var subQ1=sQuery(id+"F5.wireOp",EDGE,"E0.left");var subQ2=makeQuery(id+"F5.imprint","INTERSECT",VERTEX,{"derivedFrom":[subQ1,subQ0]});Q27=makeQuery(id+"F5.imprint","IMPRINT",FACE,{"disambiguationData":[TD([[makeQuery(id+"F5.imprint","IMPRINT",EDGE,{"disambiguationData":[TD([[subQ2,-1.0]])],"derivedFrom":subQ1}),-1.0]])]});}
            var Q28;
            {var subQ7=sQuery(id+"F5.wireOp",EDGE,"E15");Q28=makeQuery(id+"F5.imprint","IMPRINT",FACE,{"disambiguationData":[TD([[makeQuery(id+"F5.imprint","IMPRINT",EDGE,{"derivedFrom":subQ7}),1.0]])]});}
            var Q29;
            {var subQ3=sQuery(id+"F5.wireOp",EDGE,"E13");Q29=makeQuery(id+"F5.imprint","IMPRINT",FACE,{"disambiguationData":[TD([[makeQuery(id+"F5.imprint","IMPRINT",EDGE,{"derivedFrom":subQ3}),-1.0]])]});}
            var Q30;
            {var subQ0=sQuery(id+"F5.wireOp",EDGE,"E18");var subQ1=sQuery(id+"F5.wireOp",EDGE,"E0.top");var subQ2=makeQuery(id+"F5.imprint","INTERSECT",VERTEX,{"derivedFrom":[subQ1,subQ0]});Q30=makeQuery(id+"F5.imprint","IMPRINT",FACE,{"disambiguationData":[TD([[makeQuery(id+"F5.imprint","IMPRINT",EDGE,{"disambiguationData":[TD([[subQ2,1.0]])],"derivedFrom":subQ1}),-1.0]])]});}
            var Q31;
            {var subQ0=sQuery(id+"F5.wireOp",EDGE,"E2");var subQ1=sQuery(id+"F5.wireOp",EDGE,"E0.top");var subQ2=makeQuery(id+"F5.imprint","INTERSECT",VERTEX,{"derivedFrom":[subQ1,subQ0]});Q31=makeQuery(id+"F5.imprint","IMPRINT",FACE,{"disambiguationData":[TD([[makeQuery(id+"F5.imprint","IMPRINT",EDGE,{"disambiguationData":[TD([[subQ2,1.0]])],"derivedFrom":subQ1}),-1.0]])]});}
            var Q32;
            {var subQ3=sQuery(id+"F5.wireOp",EDGE,"E12");Q32=makeQuery(id+"F5.imprint","IMPRINT",FACE,{"disambiguationData":[TD([[makeQuery(id+"F5.imprint","IMPRINT",EDGE,{"derivedFrom":subQ3}),1.0]])]});}
            var Q33;
            {var subQ0=sQuery(id+"F5.wireOp",EDGE,"E13");Q33=makeQuery(id+"F5.imprint","IMPRINT",FACE,{"disambiguationData":[TD([[makeQuery(id+"F5.imprint","IMPRINT",EDGE,{"derivedFrom":subQ0}),1.0]])]});}
            var Q34;
            {var subQ0=sQuery(id+"F5.wireOp",EDGE,"E12");Q34=makeQuery(id+"F5.imprint","IMPRINT",FACE,{"disambiguationData":[TD([[makeQuery(id+"F5.imprint","IMPRINT",EDGE,{"derivedFrom":subQ0}),-1.0]])]});}
            var Q35;
            {var subQ0=sQuery(id+"F5.wireOp",EDGE,"E6");var subQ1=sQuery(id+"F5.wireOp",EDGE,"E0.right");var subQ2=makeQuery(id+"F5.imprint","INTERSECT",VERTEX,{"derivedFrom":[subQ1,subQ0]});Q35=makeQuery(id+"F5.imprint","IMPRINT",FACE,{"disambiguationData":[TD([[makeQuery(id+"F5.imprint","IMPRINT",EDGE,{"disambiguationData":[TD([[subQ2,-1.0]])],"derivedFrom":subQ1}),1.0]])]});}
            var Q36;
            {var subQ6=sQuery(id+"F5.wireOp",EDGE,"E14");Q36=makeQuery(id+"F5.imprint","IMPRINT",FACE,{"disambiguationData":[TD([[makeQuery(id+"F5.imprint","IMPRINT",EDGE,{"derivedFrom":subQ6}),1.0]])]});}
            var Q37;
            {var subQ3=sQuery(id+"F5.wireOp",EDGE,"E15");Q37=makeQuery(id+"F5.imprint","IMPRINT",FACE,{"disambiguationData":[TD([[makeQuery(id+"F5.imprint","IMPRINT",EDGE,{"derivedFrom":subQ3}),-1.0]])]});}
            var Q38;
            {var subQ0=sQuery(id+"F5.wireOp",EDGE,"E18");var subQ1=sQuery(id+"F5.wireOp",EDGE,"E0.bottom");var subQ2=makeQuery(id+"F5.imprint","INTERSECT",VERTEX,{"derivedFrom":[subQ1,subQ0]});Q38=makeQuery(id+"F5.imprint","IMPRINT",FACE,{"disambiguationData":[TD([[makeQuery(id+"F5.imprint","IMPRINT",EDGE,{"disambiguationData":[TD([[subQ2,1.0]])],"derivedFrom":subQ1}),1.0]])]});}
            var Q39;
            {var subQ0=sQuery(id+"F5.wireOp",EDGE,"E4");var subQ1=sQuery(id+"F5.wireOp",EDGE,"E1");var subQ2=makeQuery(id+"F5.imprint","INTERSECT",VERTEX,{"derivedFrom":[subQ1,subQ0]});Q39=makeQuery(id+"F5.imprint","IMPRINT",FACE,{"disambiguationData":[TD([[makeQuery(id+"F5.imprint","IMPRINT",EDGE,{"disambiguationData":[TD([[subQ2,-1.0]])],"derivedFrom":subQ1}),-1.0]])]});}
            var Q40;
            {var subQ0=sQuery(id+"F5.wireOp",EDGE,"E2");var subQ1=sQuery(id+"F5.wireOp",EDGE,"E0.bottom");var subQ2=makeQuery(id+"F5.imprint","INTERSECT",VERTEX,{"derivedFrom":[subQ1,subQ0]});Q40=makeQuery(id+"F5.imprint","IMPRINT",FACE,{"disambiguationData":[TD([[makeQuery(id+"F5.imprint","IMPRINT",EDGE,{"disambiguationData":[TD([[subQ2,1.0]])],"derivedFrom":subQ1}),1.0]])]});}
            var Q41;
            {var subQ0=sQuery(id+"F5.wireOp",EDGE,"E1");var subQ1=sQuery(id+"F5.wireOp",EDGE,"E0.bottom");var subQ2=makeQuery(id+"F5.imprint","INTERSECT",VERTEX,{"derivedFrom":[subQ1,subQ0]});Q41=makeQuery(id+"F5.imprint","IMPRINT",FACE,{"disambiguationData":[TD([[makeQuery(id+"F5.imprint","IMPRINT",EDGE,{"disambiguationData":[TD([[subQ2,1.0]])],"derivedFrom":subQ1}),1.0]])]});}
            var Q42;
            {var subQ0=sQuery(id+"F5.wireOp",EDGE,"E18");var subQ1=sQuery(id+"F5.wireOp",EDGE,"E3.bottom");var subQ2=makeQuery(id+"F5.imprint","INTERSECT",VERTEX,{"derivedFrom":[subQ1,subQ0]});Q42=makeQuery(id+"F5.imprint","IMPRINT",FACE,{"disambiguationData":[TD([[makeQuery(id+"F5.imprint","IMPRINT",EDGE,{"disambiguationData":[TD([[subQ2,-1.0]])],"derivedFrom":subQ1}),-1.0]])]});}
            var Q43;
            {var subQ0=sQuery(id+"F5.wireOp",EDGE,"E4");var subQ1=sQuery(id+"F5.wireOp",EDGE,"E0.left");var subQ2=makeQuery(id+"F5.imprint","INTERSECT",VERTEX,{"derivedFrom":[subQ1,subQ0]});Q43=makeQuery(id+"F5.imprint","IMPRINT",FACE,{"disambiguationData":[TD([[makeQuery(id+"F5.imprint","IMPRINT",EDGE,{"disambiguationData":[TD([[subQ2,-1.0]])],"derivedFrom":subQ1}),-1.0]])]});}
            var Q44;
            {var subQ0=sQuery(id+"F5.wireOp",EDGE,"E4");var subQ1=sQuery(id+"F5.wireOp",EDGE,"E0.left");var subQ2=makeQuery(id+"F5.imprint","INTERSECT",VERTEX,{"derivedFrom":[subQ1,subQ0]});Q44=makeQuery(id+"F5.imprint","IMPRINT",FACE,{"disambiguationData":[TD([[makeQuery(id+"F5.imprint","IMPRINT",EDGE,{"disambiguationData":[TD([[subQ2,1.0]])],"derivedFrom":subQ1}),-1.0]])]});}
            var Q45;
            {var subQ1=sQuery(id+"F5.wireOp",EDGE,"E3.bottom");var subQ3=sQuery(id+"F5.wireOp",EDGE,"E19");var subQ4=makeQuery(id+"F5.imprint","INTERSECT",VERTEX,{"derivedFrom":[subQ1,subQ3]});Q45=makeQuery(id+"F5.imprint","IMPRINT",FACE,{"disambiguationData":[TD([[makeQuery(id+"F5.imprint","IMPRINT",EDGE,{"disambiguationData":[TD([[subQ4,-1.0]])],"derivedFrom":subQ3}),1.0]])]});}
            var Q46;
            {var subQ0=sQuery(id+"F5.wireOp",EDGE,"E22");var subQ1=sQuery(id+"F5.wireOp",EDGE,"E1");var subQ2=makeQuery(id+"F5.imprint","INTERSECT",VERTEX,{"derivedFrom":[subQ1,subQ0]});Q46=makeQuery(id+"F5.imprint","IMPRINT",FACE,{"disambiguationData":[TD([[makeQuery(id+"F5.imprint","IMPRINT",EDGE,{"disambiguationData":[TD([[subQ2,-1.0]])],"derivedFrom":subQ1}),1.0]])]});}
            var Q47;
            {var subQ0=sQuery(id+"F5.wireOp",EDGE,"E22");var subQ1=sQuery(id+"F5.wireOp",EDGE,"E2");var subQ2=makeQuery(id+"F5.imprint","INTERSECT",VERTEX,{"derivedFrom":[subQ1,subQ0]});Q47=makeQuery(id+"F5.imprint","IMPRINT",FACE,{"disambiguationData":[TD([[makeQuery(id+"F5.imprint","IMPRINT",EDGE,{"disambiguationData":[TD([[subQ2,-1.0]])],"derivedFrom":subQ1}),-1.0]])]});}
            var Q48;
            {var subQ0=sQuery(id+"F5.wireOp",EDGE,"E4");var subQ1=sQuery(id+"F5.wireOp",EDGE,"E0.right");var subQ2=makeQuery(id+"F5.imprint","INTERSECT",VERTEX,{"derivedFrom":[subQ1,subQ0]});Q48=makeQuery(id+"F5.imprint","IMPRINT",FACE,{"disambiguationData":[TD([[makeQuery(id+"F5.imprint","IMPRINT",EDGE,{"disambiguationData":[TD([[subQ2,1.0]])],"derivedFrom":subQ1}),1.0]])]});}
            var Q49;
            {var subQ0=sQuery(id+"F5.wireOp",EDGE,"E22");var subQ1=sQuery(id+"F5.wireOp",EDGE,"E1");var subQ2=makeQuery(id+"F5.imprint","INTERSECT",VERTEX,{"derivedFrom":[subQ1,subQ0]});Q49=makeQuery(id+"F5.imprint","IMPRINT",FACE,{"disambiguationData":[TD([[makeQuery(id+"F5.imprint","IMPRINT",EDGE,{"disambiguationData":[TD([[subQ2,-1.0]])],"derivedFrom":subQ1}),-1.0]])]});}
            var Q50;
            {var subQ0=sQuery(id+"F5.wireOp",EDGE,"E18");var subQ1=sQuery(id+"F5.wireOp",EDGE,"E4");var subQ2=makeQuery(id+"F5.imprint","INTERSECT",VERTEX,{"derivedFrom":[subQ1,subQ0]});Q50=makeQuery(id+"F5.imprint","IMPRINT",FACE,{"disambiguationData":[TD([[makeQuery(id+"F5.imprint","IMPRINT",EDGE,{"disambiguationData":[TD([[subQ2,-1.0]])],"derivedFrom":subQ1}),1.0]])]});}
            extrude(context, id + "F12", {"entities" : qUnion([Q0, Q1, Q2, Q3, Q4, Q5, Q6, Q7, Q8, Q9, Q10, Q11, Q12, Q13, Q14, Q15, Q16, Q17, Q18, Q19, Q20, Q21, Q22, Q23, Q24, Q25, Q26, Q27, Q28, Q29, Q30, Q31, Q32, Q33, Q34, Q35, Q36, Q37, Q38, Q39, Q40, Q41, Q42, Q43, Q44, Q45, Q46, Q47, Q48, Q49, Q50]), "oppositeDirection" : true, "depth" : getVariable(context, 'thickwood'), "offsetDistance" : 25.4 * mm});
        }
        {
            var Q0;
            {var subQ0=sQuery(id+"F5.wireOp",EDGE,"E22");var subQ1=sQuery(id+"F5.wireOp",EDGE,"E3.right");var subQ2=makeQuery(id+"F5.imprint","INTERSECT",VERTEX,{"derivedFrom":[subQ1,subQ0]});Q0=makeQuery(id+"F5.imprint","IMPRINT",FACE,{"disambiguationData":[TD([[makeQuery(id+"F5.imprint","IMPRINT",EDGE,{"disambiguationData":[TD([[subQ2,-1.0]])],"derivedFrom":subQ1}),-1.0]])]});}
            var Q1;
            {var subQ0=sQuery(id+"F5.wireOp",EDGE,"E18");var subQ1=sQuery(id+"F5.wireOp",EDGE,"E4");var subQ2=makeQuery(id+"F5.imprint","INTERSECT",VERTEX,{"derivedFrom":[subQ1,subQ0]});Q1=makeQuery(id+"F5.imprint","IMPRINT",FACE,{"disambiguationData":[TD([[makeQuery(id+"F5.imprint","IMPRINT",EDGE,{"disambiguationData":[TD([[subQ2,-1.0]])],"derivedFrom":subQ1}),1.0]])]});}
            var Q2;
            {var subQ0=sQuery(id+"F5.wireOp",EDGE,"E4");var subQ1=sQuery(id+"F5.wireOp",EDGE,"E2");var subQ2=makeQuery(id+"F5.imprint","INTERSECT",VERTEX,{"derivedFrom":[subQ1,subQ0]});Q2=makeQuery(id+"F5.imprint","IMPRINT",FACE,{"disambiguationData":[TD([[makeQuery(id+"F5.imprint","IMPRINT",EDGE,{"disambiguationData":[TD([[subQ2,-1.0]])],"derivedFrom":subQ1}),-1.0]])]});}
            var Q3;
            {var subQ0=sQuery(id+"F5.wireOp",EDGE,"E4");var subQ1=sQuery(id+"F5.wireOp",EDGE,"E1");var subQ2=makeQuery(id+"F5.imprint","INTERSECT",VERTEX,{"derivedFrom":[subQ1,subQ0]});Q3=makeQuery(id+"F5.imprint","IMPRINT",FACE,{"disambiguationData":[TD([[makeQuery(id+"F5.imprint","IMPRINT",EDGE,{"disambiguationData":[TD([[subQ2,-1.0]])],"derivedFrom":subQ1}),-1.0]])]});}
            var Q4;
            {var subQ0=sQuery(id+"F5.wireOp",EDGE,"E4");var subQ1=sQuery(id+"F5.wireOp",EDGE,"E1");var subQ2=makeQuery(id+"F5.imprint","INTERSECT",VERTEX,{"derivedFrom":[subQ1,subQ0]});Q4=makeQuery(id+"F5.imprint","IMPRINT",FACE,{"disambiguationData":[TD([[makeQuery(id+"F5.imprint","IMPRINT",EDGE,{"disambiguationData":[TD([[subQ2,-1.0]])],"derivedFrom":subQ1}),1.0]])]});}
            extrude(context, id + "F13", {"entities" : qUnion([Q0, Q1, Q2, Q3, Q4]), "depth" : getVariable(context, 'cartwidth') - getVariable(context, 'thickwood'), "offsetDistance" : 25.4 * mm});
        }
        {
            var Q0;
            Q0=makeQuery(id+"F7.opExtrude","SWEPT_FACE",FACE,{"disambiguationData":[OSD([sQuery(id+"F5.wireOp",EDGE,"E3.left")])]});
            var sketch = newSketch(context, id + "F14", { "sketchPlane" : qUnion([Q0])});
            skLineSegment(sketch, "E23", {"start": v(-596.9, 249) * mm, "end": v(-596.9, 172.8) * mm});
            skLineSegment(sketch, "E24", {"start": v(-596.9, 172.8) * mm, "end": v(-573.33, 172.8) * mm});
            skLineSegment(sketch, "E25", {"start": v(-573.33, 172.8) * mm, "end": v(-573.33, 249) * mm});
            skLineSegment(sketch, "E26", {"start": v(-573.33, 249) * mm, "end": v(-596.9, 249) * mm});
            skSolve(sketch);
        }
        {
            var Q0;
            Q0=makeQuery(id+"F14.imprint","IMPRINT",FACE,{"disambiguationData":[TD([[makeQuery(id+"F14.imprint","IMPRINT",EDGE,{"derivedFrom":sQuery(id+"F14.wireOp",EDGE,"E23")}),1.0]])]});
            extrude(context, id + "F15", {"entities" : qUnion([Q0]), "depth" : getVariable(context, 'cartlength') - 2 * (getVariable(context, 'thickwood')), "offsetDistance" : 25.4 * mm});
        }
        {
            var Q0;
            {var subQ0=sQuery(id+"F5.wireOp",EDGE,"E5");var subQ1=sQuery(id+"F5.wireOp",EDGE,"E1");var subQ2=makeQuery(id+"F5.imprint","INTERSECT",VERTEX,{"derivedFrom":[subQ1,subQ0]});Q0=makeQuery(id+"F5.imprint","IMPRINT",FACE,{"disambiguationData":[TD([[makeQuery(id+"F5.imprint","IMPRINT",EDGE,{"disambiguationData":[TD([[subQ2,-1.0]])],"derivedFrom":subQ1}),1.0]])]});}
            var Q1;
            {var subQ0=sQuery(id+"F5.wireOp",EDGE,"E7");var subQ1=sQuery(id+"F5.wireOp",EDGE,"E1");var subQ2=makeQuery(id+"F5.imprint","INTERSECT",VERTEX,{"derivedFrom":[subQ1,subQ0]});Q1=makeQuery(id+"F5.imprint","IMPRINT",FACE,{"disambiguationData":[TD([[makeQuery(id+"F5.imprint","IMPRINT",EDGE,{"disambiguationData":[TD([[subQ2,-1.0]])],"derivedFrom":subQ1}),1.0]])]});}
            var Q2;
            {var subQ0=sQuery(id+"F5.wireOp",EDGE,"E5");var subQ1=sQuery(id+"F5.wireOp",EDGE,"E2");var subQ2=makeQuery(id+"F5.imprint","INTERSECT",VERTEX,{"derivedFrom":[subQ1,subQ0]});Q2=makeQuery(id+"F5.imprint","IMPRINT",FACE,{"disambiguationData":[TD([[makeQuery(id+"F5.imprint","IMPRINT",EDGE,{"disambiguationData":[TD([[subQ2,-1.0]])],"derivedFrom":subQ1}),-1.0]])]});}
            var Q3;
            {var subQ0=sQuery(id+"F5.wireOp",EDGE,"E7");var subQ1=sQuery(id+"F5.wireOp",EDGE,"E2");var subQ2=makeQuery(id+"F5.imprint","INTERSECT",VERTEX,{"derivedFrom":[subQ1,subQ0]});Q3=makeQuery(id+"F5.imprint","IMPRINT",FACE,{"disambiguationData":[TD([[makeQuery(id+"F5.imprint","IMPRINT",EDGE,{"disambiguationData":[TD([[subQ2,-1.0]])],"derivedFrom":subQ1}),-1.0]])]});}
            var Q4;
            {var subQ0=sQuery(id+"F5.wireOp",EDGE,"E4");var subQ1=sQuery(id+"F5.wireOp",EDGE,"E3.right");var subQ2=makeQuery(id+"F5.imprint","INTERSECT",VERTEX,{"derivedFrom":[subQ1,subQ0]});Q4=makeQuery(id+"F5.imprint","IMPRINT",FACE,{"disambiguationData":[TD([[makeQuery(id+"F5.imprint","IMPRINT",EDGE,{"disambiguationData":[TD([[subQ2,-1.0]])],"derivedFrom":subQ1}),-1.0]])]});}
            var Q5;
            {var subQ0=sQuery(id+"F5.wireOp",EDGE,"E7");var subQ1=sQuery(id+"F5.wireOp",EDGE,"E3.right");var subQ2=makeQuery(id+"F5.imprint","INTERSECT",VERTEX,{"derivedFrom":[subQ1,subQ0]});Q5=makeQuery(id+"F5.imprint","IMPRINT",FACE,{"disambiguationData":[TD([[makeQuery(id+"F5.imprint","IMPRINT",EDGE,{"disambiguationData":[TD([[subQ2,1.0]])],"derivedFrom":subQ1}),-1.0]])]});}
            extrude(context, id + "F16", {"entities" : qUnion([Q0, Q1, Q2, Q3, Q4, Q5]), "depth" : getVariable(context, 'drawerdepth'), "offsetDistance" : 25.4 * mm});
        }
        {
            var Q0;
            {var subQ0=sQuery(id+"F5.wireOp",EDGE,"E4");Q0=makeQuery(id+"F16.opExtrude","SWEPT_FACE",FACE,{"disambiguationData":[OSD([subQ0]),TDD([makeQuery(id+"F5.imprint","IMPRINT",EDGE,{"disambiguationData":[TD([[makeQuery(id+"F5.imprint","INTERSECT",VERTEX,{"derivedFrom":[sQuery(id+"F5.wireOp",EDGE,"E1"),subQ0]}),1.0]])],"derivedFrom":subQ0})])]});}
            var Q1;
            {var subQ0=sQuery(id+"F5.wireOp",EDGE,"E4");Q1=makeQuery(id+"F16.opExtrude","SWEPT_FACE",FACE,{"disambiguationData":[OSD([subQ0]),TDD([makeQuery(id+"F5.imprint","IMPRINT",EDGE,{"disambiguationData":[TD([[makeQuery(id+"F5.imprint","INTERSECT",VERTEX,{"derivedFrom":[sQuery(id+"F5.wireOp",EDGE,"E2"),subQ0]}),-1.0]])],"derivedFrom":subQ0})])]});}
            var Q2;
            {var subQ0=sQuery(id+"F5.wireOp",EDGE,"E4");Q2=makeQuery(id+"F16.opExtrude","SWEPT_FACE",FACE,{"disambiguationData":[OSD([subQ0]),TDD([makeQuery(id+"F5.imprint","IMPRINT",EDGE,{"disambiguationData":[TD([[makeQuery(id+"F5.imprint","INTERSECT",VERTEX,{"derivedFrom":[sQuery(id+"F5.wireOp",EDGE,"E3.right"),subQ0]}),1.0]])],"derivedFrom":subQ0})])]});}
            var Q3;
            {var subQ0=sQuery(id+"F5.wireOp",EDGE,"E6");Q3=makeQuery(id+"F16.opExtrude","SWEPT_FACE",FACE,{"disambiguationData":[OSD([subQ0]),TDD([makeQuery(id+"F5.imprint","IMPRINT",EDGE,{"disambiguationData":[TD([[makeQuery(id+"F5.imprint","INTERSECT",VERTEX,{"derivedFrom":[sQuery(id+"F5.wireOp",EDGE,"E1"),subQ0]}),1.0]])],"derivedFrom":subQ0})])]});}
            var Q4;
            {var subQ0=sQuery(id+"F5.wireOp",EDGE,"E6");Q4=makeQuery(id+"F16.opExtrude","SWEPT_FACE",FACE,{"disambiguationData":[OSD([subQ0]),TDD([makeQuery(id+"F5.imprint","IMPRINT",EDGE,{"disambiguationData":[TD([[makeQuery(id+"F5.imprint","INTERSECT",VERTEX,{"derivedFrom":[sQuery(id+"F5.wireOp",EDGE,"E2"),subQ0]}),-1.0]])],"derivedFrom":subQ0})])]});}
            var Q5;
            {var subQ0=sQuery(id+"F5.wireOp",EDGE,"E6");Q5=makeQuery(id+"F16.opExtrude","SWEPT_FACE",FACE,{"disambiguationData":[OSD([subQ0]),TDD([makeQuery(id+"F5.imprint","IMPRINT",EDGE,{"disambiguationData":[TD([[makeQuery(id+"F5.imprint","INTERSECT",VERTEX,{"derivedFrom":[sQuery(id+"F5.wireOp",EDGE,"E3.right"),subQ0]}),1.0]])],"derivedFrom":subQ0})])]});}
            shell(context, id + "F17", {"entities" : qUnion([Q0, Q1, Q2, Q3, Q4, Q5]), "thickness" : getVariable(context, 'thinwood')});
        }
        {
            var Q0;
            {var subQ0=sQuery(id+"F5.wireOp",EDGE,"E5");var subQ1=sQuery(id+"F5.wireOp",EDGE,"E3.right");var subQ2=makeQuery(id+"F5.imprint","INTERSECT",VERTEX,{"derivedFrom":[subQ1,subQ0]});Q0=makeQuery(id+"F5.imprint","IMPRINT",FACE,{"disambiguationData":[TD([[makeQuery(id+"F5.imprint","IMPRINT",EDGE,{"disambiguationData":[TD([[subQ2,-1.0]])],"derivedFrom":subQ1}),-1.0]])]});}
            var Q1;
            {var subQ0=sQuery(id+"F5.wireOp",EDGE,"E6");var subQ1=sQuery(id+"F5.wireOp",EDGE,"E2");var subQ2=makeQuery(id+"F5.imprint","INTERSECT",VERTEX,{"derivedFrom":[subQ1,subQ0]});Q1=makeQuery(id+"F5.imprint","IMPRINT",FACE,{"disambiguationData":[TD([[makeQuery(id+"F5.imprint","IMPRINT",EDGE,{"disambiguationData":[TD([[subQ2,-1.0]])],"derivedFrom":subQ1}),-1.0]])]});}
            var Q2;
            {var subQ0=sQuery(id+"F5.wireOp",EDGE,"E6");var subQ1=sQuery(id+"F5.wireOp",EDGE,"E1");var subQ2=makeQuery(id+"F5.imprint","INTERSECT",VERTEX,{"derivedFrom":[subQ1,subQ0]});Q2=makeQuery(id+"F5.imprint","IMPRINT",FACE,{"disambiguationData":[TD([[makeQuery(id+"F5.imprint","IMPRINT",EDGE,{"disambiguationData":[TD([[subQ2,-1.0]])],"derivedFrom":subQ1}),1.0]])]});}
            var Q3;
            {var subQ0=sQuery(id+"F5.wireOp",EDGE,"E11");var subQ1=sQuery(id+"F5.wireOp",EDGE,"E1");var subQ2=makeQuery(id+"F5.imprint","INTERSECT",VERTEX,{"derivedFrom":[subQ1,subQ0]});Q3=makeQuery(id+"F5.imprint","IMPRINT",FACE,{"disambiguationData":[TD([[makeQuery(id+"F5.imprint","IMPRINT",EDGE,{"disambiguationData":[TD([[subQ2,-1.0]])],"derivedFrom":subQ1}),1.0]])]});}
            var Q4;
            {var subQ0=sQuery(id+"F5.wireOp",EDGE,"E11");var subQ1=sQuery(id+"F5.wireOp",EDGE,"E2");var subQ2=makeQuery(id+"F5.imprint","INTERSECT",VERTEX,{"derivedFrom":[subQ1,subQ0]});Q4=makeQuery(id+"F5.imprint","IMPRINT",FACE,{"disambiguationData":[TD([[makeQuery(id+"F5.imprint","IMPRINT",EDGE,{"disambiguationData":[TD([[subQ2,-1.0]])],"derivedFrom":subQ1}),-1.0]])]});}
            var Q5;
            {var subQ1=sQuery(id+"F5.wireOp",EDGE,"E3.right");var subQ3=sQuery(id+"F5.wireOp",EDGE,"E7");var subQ4=makeQuery(id+"F5.imprint","INTERSECT",VERTEX,{"derivedFrom":[subQ1,subQ3]});Q5=makeQuery(id+"F5.imprint","IMPRINT",FACE,{"disambiguationData":[TD([[makeQuery(id+"F5.imprint","IMPRINT",EDGE,{"disambiguationData":[TD([[subQ4,1.0]])],"derivedFrom":subQ3}),-1.0]])]});}
            extrude(context, id + "F18", {"entities" : qUnion([Q0, Q1, Q2, Q3, Q4, Q5]), "depth" : getVariable(context, 'drawerdepth'), "offsetDistance" : 25.4 * mm});
        }
        {
            var Q0;
            {var subQ0=sQuery(id+"F5.wireOp",EDGE,"E5");Q0=makeQuery(id+"F18.opExtrude","SWEPT_FACE",FACE,{"disambiguationData":[OSD([subQ0]),TDD([makeQuery(id+"F5.imprint","IMPRINT",EDGE,{"disambiguationData":[TD([[makeQuery(id+"F5.imprint","INTERSECT",VERTEX,{"derivedFrom":[sQuery(id+"F5.wireOp",EDGE,"E1"),subQ0]}),1.0]])],"derivedFrom":subQ0})])]});}
            var Q1;
            {var subQ0=sQuery(id+"F5.wireOp",EDGE,"E5");Q1=makeQuery(id+"F18.opExtrude","SWEPT_FACE",FACE,{"disambiguationData":[OSD([subQ0]),TDD([makeQuery(id+"F5.imprint","IMPRINT",EDGE,{"disambiguationData":[TD([[makeQuery(id+"F5.imprint","INTERSECT",VERTEX,{"derivedFrom":[sQuery(id+"F5.wireOp",EDGE,"E2"),subQ0]}),-1.0]])],"derivedFrom":subQ0})])]});}
            var Q2;
            {var subQ0=sQuery(id+"F5.wireOp",EDGE,"E5");Q2=makeQuery(id+"F18.opExtrude","SWEPT_FACE",FACE,{"disambiguationData":[OSD([subQ0]),TDD([makeQuery(id+"F5.imprint","IMPRINT",EDGE,{"disambiguationData":[TD([[makeQuery(id+"F5.imprint","INTERSECT",VERTEX,{"derivedFrom":[sQuery(id+"F5.wireOp",EDGE,"E3.right"),subQ0]}),1.0]])],"derivedFrom":subQ0})])]});}
            var Q3;
            {var subQ0=sQuery(id+"F5.wireOp",EDGE,"E7");Q3=makeQuery(id+"F18.opExtrude","SWEPT_FACE",FACE,{"disambiguationData":[OSD([subQ0]),TDD([makeQuery(id+"F5.imprint","IMPRINT",EDGE,{"disambiguationData":[TD([[makeQuery(id+"F5.imprint","INTERSECT",VERTEX,{"derivedFrom":[sQuery(id+"F5.wireOp",EDGE,"E1"),subQ0]}),1.0]])],"derivedFrom":subQ0})])]});}
            var Q4;
            {var subQ0=sQuery(id+"F5.wireOp",EDGE,"E7");Q4=makeQuery(id+"F18.opExtrude","SWEPT_FACE",FACE,{"disambiguationData":[OSD([subQ0]),TDD([makeQuery(id+"F5.imprint","IMPRINT",EDGE,{"disambiguationData":[TD([[makeQuery(id+"F5.imprint","INTERSECT",VERTEX,{"derivedFrom":[sQuery(id+"F5.wireOp",EDGE,"E2"),subQ0]}),-1.0]])],"derivedFrom":subQ0})])]});}
            var Q5;
            {var subQ0=sQuery(id+"F5.wireOp",EDGE,"E7");Q5=makeQuery(id+"F18.opExtrude","SWEPT_FACE",FACE,{"disambiguationData":[OSD([subQ0]),TDD([makeQuery(id+"F5.imprint","IMPRINT",EDGE,{"disambiguationData":[TD([[makeQuery(id+"F5.imprint","INTERSECT",VERTEX,{"derivedFrom":[sQuery(id+"F5.wireOp",EDGE,"E3.right"),subQ0]}),1.0]])],"derivedFrom":subQ0})])]});}
            shell(context, id + "F19", {"entities" : qUnion([Q0, Q1, Q2, Q3, Q4, Q5]), "thickness" : getVariable(context, 'thinwood')});
        }
    });
